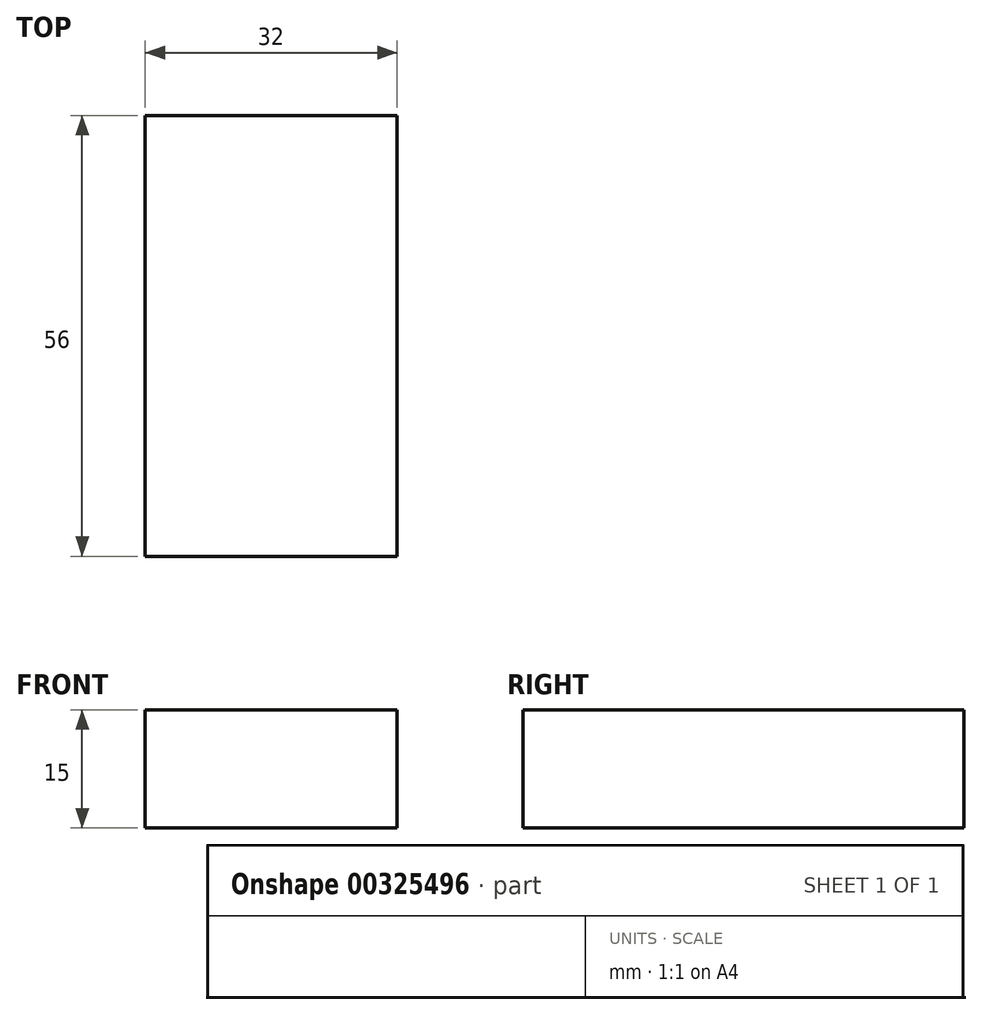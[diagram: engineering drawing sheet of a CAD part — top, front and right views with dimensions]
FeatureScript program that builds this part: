
annotation { "Feature Type Name" : "Feature", "Feature Type Description" : "" }
export const myFeature = defineFeature(function(context is Context, id is Id, definition is map)
    precondition{}
    {
        {
            var Q0;
            Q0=qCreatedBy(makeId("Top.planeOp"),FACE);
            var sketch = newSketch(context, id + "F0", { "sketchPlane" : qUnion([Q0])});
            skLineSegment(sketch, "E0.bottom", {"start": v(16, 28) * mm, "end": v(-16, 28) * mm});
            skLineSegment(sketch, "E0.top", {"start": v(16, -28) * mm, "end": v(-16, -28) * mm});
            skLineSegment(sketch, "E0.left", {"start": v(16, 28) * mm, "end": v(16, -28) * mm});
            skLineSegment(sketch, "E0.right", {"start": v(-16, 28) * mm, "end": v(-16, -28) * mm});
            skPoint(sketch, "E0.middle", {"position": v(0, 0) * mm});
            skSolve(sketch);
        }
        {
            var Q0;
            Q0 = qSketchRegion(id + "F0", true);
            extrude(context, id + "F1", {"entities" : qUnion([Q0]), "depth" : 15 * mm});
        }
    });
